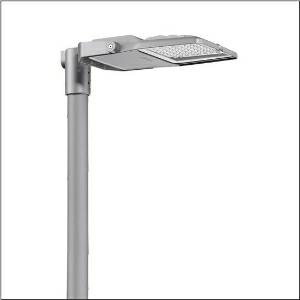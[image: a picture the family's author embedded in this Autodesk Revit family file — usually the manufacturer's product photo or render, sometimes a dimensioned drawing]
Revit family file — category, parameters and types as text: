
# Revit family: floodlight_fl_21_mini___pl61_5xa7772b4c3a_5b6b
name_source: partatom
category: Lighting Fixtures
units: mm (PartAtom-declared; Revit-internal decimal feet)

## family parameters
Cut with Voids When Loaded = No
Host = Face
Light Source = No
Part Type = Normal
Room Calculation Point = No
Round Connector Dimension = Use Diameter
Shared = No

## types (1)
- --- (1 x LED, 6370 lm, 45.5 W, 4000K)
    Apparent Load = 46 VA
    CIE Flux Codes = 33 65 98 100 100
    Color Rendering = 70
    Color Temperature = 4000K
    Default Elevation = 1800 mm
    Description = Floodlight FL 21 mini, floodlight, primary light control with lens, of PMMA, primary optical cover: protective disc, of toughened safety glass, transparent, light distribution: PL61, light emission: direct distribution, installation type: surface-mounted, LED, High Power LED, rated luminous flux: 6.370lm, luminous efficacy: 140lm/W, light colour: 740, colour temperature: 4000K, control gear: ECG iQ, control: Auto-Match, Temp-Guard, Night-Set, Smart-Wire, Desk-Remote (wireless, voltage-free reading and setting of iQ features in the workshop via application-optimized NFC function/RFID function), optimised constant luminous flux control (CLO 2.0), Light-Fading, Lumen-Switch, with terminal, 6-pole, mains connection: 220..240V, AC, 50/60Hz, start of lifetime: 46W, end of lifetime: 48W, reduction: 22W, luminaire housing, of diecast aluminium, powder-coated, Siteco® metallic grey (DB 702S), corrosivity category C5 according to DIN EN ISO 12944, mast bracket, of steel, galvanised, powder-coated, protection rating (complete): IP66, insulation class (complete): insulation class II (safety insulation), certification: CE, ENEC, VDE, protection symbol: D, impact resistance: IK08, permissible operating ambient temperature: -40..+40°C, permissible operating ambient temperature for outdoor applications: -40..+50°C, standard: DIN EN 12944, packaging unit: 1 piece

Light Distribution: PL61
    Height = 70 mm
    Lamp = 1 x LED
    Lamp Light Flux = 6370 lm
    Lamp Power = 45.5 W
    Lamp count = 1
    Length = 485 mm
    Luminous efficacy = 140 lm/W
    Manufacturer = Siteco
    ModVariant = No
    Model = 5XA7772B4C3A
    Number of Poles = 1
    OnlyDefault = Yes
    Power Factor = 1
    Product Name = Floodlight FL 21 mini | PL61
    Product group = floodlight | pylon top
    ProductGroupID = 6101
    Protection Class = Protection class II
    Protection Degree = IP 66
    RLX_Detail_Level = 1
    RlxData = <blob elided: 101169 chars, md5=083ad914>
    Socket = socket
    Standby Power = 0 W
    System Light Flux = 6370 lm
    System Power = 46 W
    Type Comments = factory setting: luminous flux: 100 % | dim-lin: 254 | 463 mA
    Type Image = l_1007125.jpg
    URL = http://relux.com
    VarID = @adj_085765
    Voltage = 0 V
    Weight = 0.00 kg
    Width = 337 mm

## geometry (parser evidence)
native form markers: Blend x4, Sweep x12
no freeform markers — native parametric forms only
